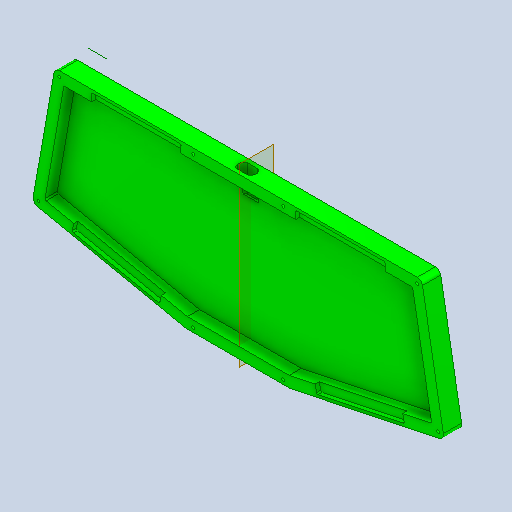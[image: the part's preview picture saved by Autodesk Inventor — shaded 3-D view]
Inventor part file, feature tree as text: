
AUTODESK INVENTOR PART (.ipt)
format: ipt  version: 2023 (Build 270158000, 158)  size: 650,240 bytes
history: native  units: mm
features: reference x28, extrude x7, sketch x7, other x6, fillet x5, plane x2, shell x1, mirror x1, hole x1, projected_geometry x1
ambient origin geometry x8: Origin, YZ Plane, XZ Plane, XY Plane, X Axis, Y Axis, Z Axis, Center Point
bodies: Body1 (feature_tree)
feature tree (59):
  extrude  "Extrusion1"  Depth=1.0mm
  shell  "Shell1"  Thickness=1.0mm
  extrude  "Extrusion7"  Depth=1.0mm
  plane  "Work Plane1"
  extrude  "Extrusion8"  Depth=17.0mm TaperAngle=0.0deg
  extrude  "Extrusion9"  Depth=8.0mm TaperAngle=0.0deg
  plane  "Work Plane2"
  extrude  "Extrusion10"  Depth=18.0mm
  mirror  "Mirror1"
  extrude  "Extrusion12"  Depth=2.0mm
  fillet  "Fillet1"  Radius=2.0mm
  fillet  "Fillet2"  Radius=2.0mm
  fillet  "Fillet3"  Radius=2.0mm
  extrude  "Extrusion13"  Depth=8.0mm TaperAngle=0.0deg
  fillet  "Fillet4"  Radius=98.02976mm
  fillet  "Fillet5"  Radius=10.0mm
  hole  "Hole1"  [1 undecoded]
  sketch  "Sketch1"  dims[d0=1.0mm d1=1.0mm d2=1.0mm]
  reference  "Reference1"
  reference  "Reference2"
  reference  "Reference3"
  reference  "Reference4"
  reference  "Reference5"
  sketch  "Sketch5"  dims[d3=1.0mm d4=1.0mm]
  projected_geometry  "Projected Loop3"
  sketch  "Sketch6"  dims[d5=1.0mm d6=17.0mm d7=0.0mm]
  sketch  "Sketch7"  dims[d8=8.0mm d19=8.0mm d20=0.0mm]
  reference  "Reference12"
  reference  "Reference13"
  reference  "Reference14"
  reference  "Reference15"
  sketch  "Sketch9"  dims[d21=14.486233mm d22=18.0mm]
  sketch  "Sketch12"  dims[d23=0.0mm d24=0.0mm d25=2.0mm d26=2.0mm d27=2.0mm d28=2.0mm]
  reference  "Reference43"
  reference  "Reference44"
  reference  "Reference45"
  reference  "Reference46"
  reference  "Reference47"
  reference  "Reference48"
  reference  "Reference49"
  reference  "Reference50"
  reference  "Reference51"
  reference  "Reference52"
  reference  "Reference53"
  reference  "Reference54"
  reference  "Reference55"
  reference  "Reference57"
  reference  "Reference59"
  reference  "Reference60"
  sketch  "Sketch13"  dims[d29=20.0mm d30=0.0mm d31=30.0mm d32=0.0mm d33=98.02976mm d40=10.0mm d41=0.0mm d42=0.0mm d43=9.0mm d44=3.0mm d45=9.0mm d48=0.5mm d50=0.5mm d51=20.5mm d52=20.5mm d53=20.5mm d56=0.5mm d57=20.5mm d58=20.5mm d60=20.5mm d61=3.0mm d62=0.0mm d63=4.0mm d64=1.0mm d65=4.0mm d66=4.0mm d68=4.0mm d69=2.2mm d70=6.0mm d71=4.0mm d72=8.0mm d73=90.0deg d74=3.0mm d75=0.0mm d78=20.5mm d80=20.5mm]
  reference  "Reference61"
  reference  "Reference63"
  reference  "Reference64"
  other  "<userpath>\Documents\Inventor\atreus-52\Assembly.iam"
  other  "Assembly.iam"
  other  "switch-plates:1"
  other  "atreus52_hotswap:1"
  other  "HRO_TYPE-C-31-M-12:1"
  other  "top-case:1"
note: 1 required parameter value undecoded (feature->parameter linkage not recoverable at this tier; creation-order binding heuristic only, values carry confidence <= 0.55)
